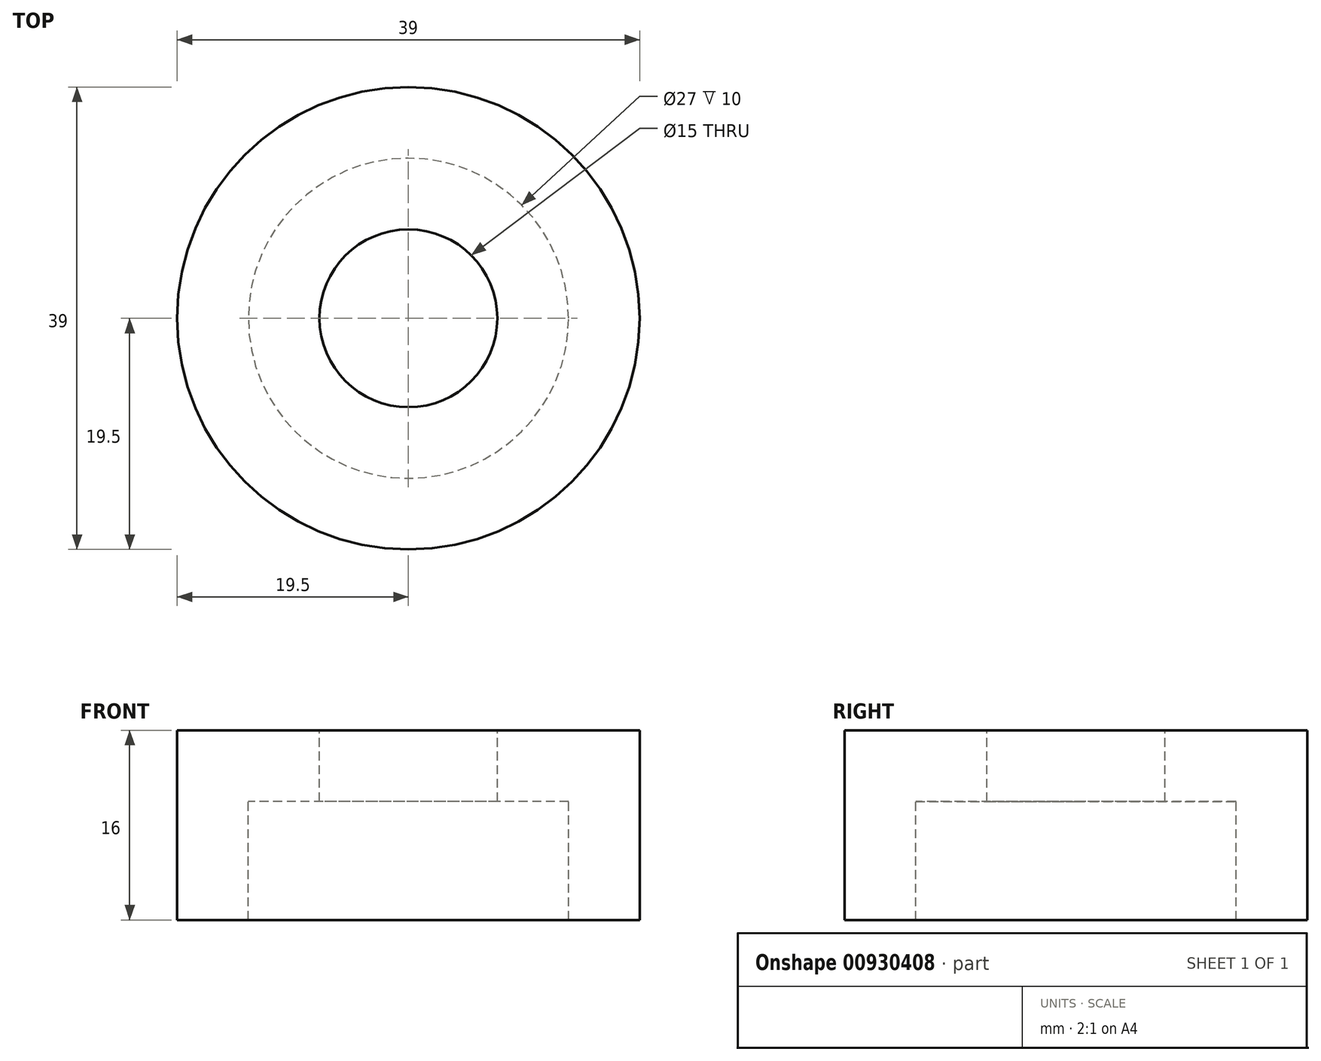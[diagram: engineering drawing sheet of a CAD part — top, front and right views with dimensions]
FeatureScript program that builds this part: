
annotation { "Feature Type Name" : "Feature", "Feature Type Description" : "" }
export const myFeature = defineFeature(function(context is Context, id is Id, definition is map)
    precondition{}
    {
        {
            var Q0;
            Q0=qCreatedBy(makeId("Front.planeOp"),FACE);
            var sketch = newSketch(context, id + "F0", { "sketchPlane" : qUnion([Q0])});
            skLineSegment(sketch, "E0", {"start": v(0, 19.38) * mm, "end": v(0, -19.07) * mm, "construction": true});
            skLineSegment(sketch, "E1", {"start": v(-19.5, -10) * mm, "end": v(-13.5, -10) * mm});
            skLineSegment(sketch, "E2", {"start": v(-13.5, -10) * mm, "end": v(-13.5, 0) * mm});
            skLineSegment(sketch, "E3", {"start": v(-13.5, 0) * mm, "end": v(-7.5, 0) * mm});
            skLineSegment(sketch, "E4", {"start": v(-7.5, 6) * mm, "end": v(-19.5, 6) * mm});
            skLineSegment(sketch, "E5", {"start": v(-19.5, 6) * mm, "end": v(-19.5, -10) * mm});
            skLineSegment(sketch, "E6", {"start": v(-7.5, 6) * mm, "end": v(-7.5, 0) * mm});
            skSolve(sketch);
        }
        {
            var Q0;
            Q0=makeQuery(id+"F0.imprint","IMPRINT",FACE,{"disambiguationData":[TD([[makeQuery(id+"F0.imprint","IMPRINT",EDGE,{"derivedFrom":sQuery(id+"F0.wireOp",EDGE,"E1")}),1.0]])]});
            var Q1;
            Q1=sQuery(id+"F0.wireOp",EDGE,"E0");
            revolve(context, id + "F1", {"surfaceOperationType" : NewSurfaceOperationType.NEW, "entities" : qUnion([Q0]), "axis" : qUnion([Q1]), "revolveType" : RevolveType.FULL});
        }
    });
